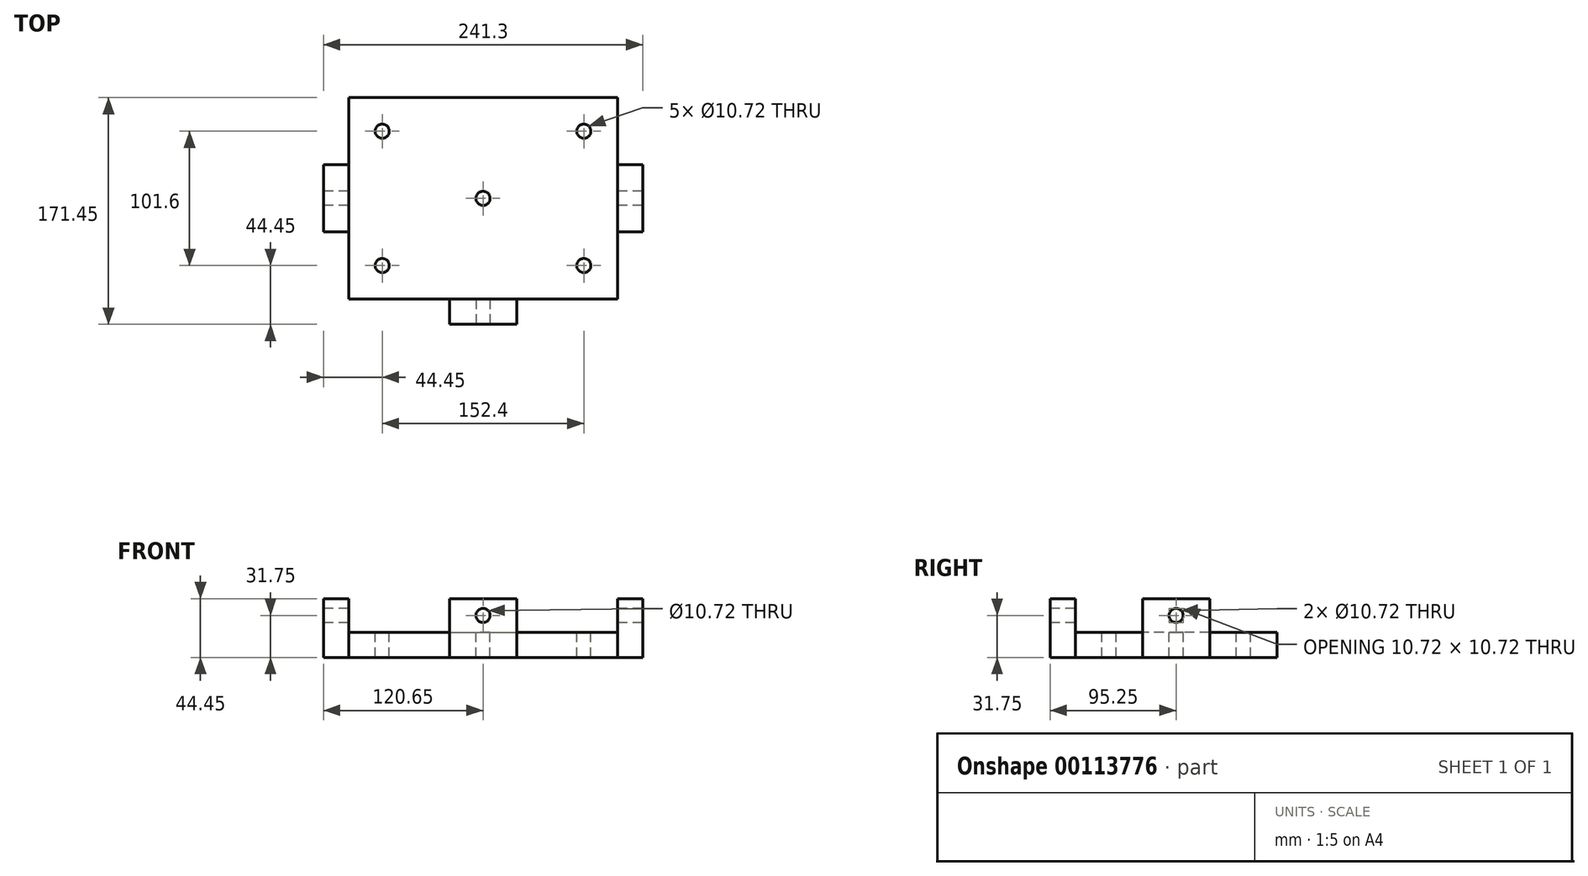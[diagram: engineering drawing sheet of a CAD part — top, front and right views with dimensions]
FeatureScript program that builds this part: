
annotation { "Feature Type Name" : "Feature", "Feature Type Description" : "" }
export const myFeature = defineFeature(function(context is Context, id is Id, definition is map)
    precondition{}
    {
        {
            var Q0;
            Q0=qCreatedBy(makeId("Top.planeOp"),FACE);
            var sketch = newSketch(context, id + "F0", { "sketchPlane" : qUnion([Q0])});
            skLineSegment(sketch, "E0.bottom", {"start": v(-101.6, 76.2) * mm, "end": v(101.6, 76.2) * mm});
            skLineSegment(sketch, "E0.top", {"start": v(-101.6, -76.2) * mm, "end": v(101.6, -76.2) * mm});
            skLineSegment(sketch, "E0.left", {"start": v(-101.6, 76.2) * mm, "end": v(-101.6, -76.2) * mm});
            skLineSegment(sketch, "E0.right", {"start": v(101.6, 76.2) * mm, "end": v(101.6, -76.2) * mm});
            skPoint(sketch, "E0.middle", {"position": v(0, 0) * mm});
            skLineSegment(sketch, "E1.bottom", {"start": v(-76.2, 50.8) * mm, "end": v(76.2, 50.8) * mm, "construction": true});
            skLineSegment(sketch, "E1.top", {"start": v(-76.2, -50.8) * mm, "end": v(76.2, -50.8) * mm, "construction": true});
            skLineSegment(sketch, "E1.left", {"start": v(-76.2, 50.8) * mm, "end": v(-76.2, -50.8) * mm, "construction": true});
            skLineSegment(sketch, "E1.right", {"start": v(76.2, 50.8) * mm, "end": v(76.2, -50.8) * mm, "construction": true});
            skSolve(sketch);
        }
        {
            var Q0;
            Q0=qSketchRegion(id+"F0",true);
            extrude(context, id + "F1", {"entities" : qUnion([Q0]), "depth" : 19.05 * mm});
        }
        {
            var Q0;
            Q0=makeQuery(id+"F1.opExtrude","CAP_FACE",FACE,{"disambiguationData":[OSD([sQuery(id+"F0.wireOp",EDGE,"E0.bottom"),sQuery(id+"F0.wireOp",EDGE,"E0.top"),sQuery(id+"F0.wireOp",EDGE,"E0.left"),sQuery(id+"F0.wireOp",EDGE,"E0.right")])],"isStart":false});
            var sketch = newSketch(context, id + "F2", { "sketchPlane" : qUnion([Q0])});
            skLineSegment(sketch, "E2.0", {"start": v(-76.2, 50.8) * mm, "end": v(76.2, 50.8) * mm, "construction": true});
            skLineSegment(sketch, "E3.0", {"start": v(-76.2, 50.8) * mm, "end": v(-76.2, -50.8) * mm, "construction": true});
            skLineSegment(sketch, "E4.0", {"start": v(-76.2, -50.8) * mm, "end": v(76.2, -50.8) * mm, "construction": true});
            skLineSegment(sketch, "E5.0", {"start": v(76.2, 50.8) * mm, "end": v(76.2, -50.8) * mm, "construction": true});
            skPoint(sketch, "E6", {"position": v(0, 0) * mm});
            skPoint(sketch, "E7", {"position": v(-76.2, 50.8) * mm});
            skPoint(sketch, "E8", {"position": v(76.2, 50.8) * mm});
            skPoint(sketch, "E9", {"position": v(76.2, -50.8) * mm});
            skPoint(sketch, "E10", {"position": v(-76.2, -50.8) * mm});
            skSolve(sketch);
        }
        {
            var Q0;
            Q0=sQuery(id+"F2.wireOp",VERTEX,"E7");
            var Q1;
            Q1=sQuery(id+"F2.wireOp",VERTEX,"E8");
            var Q2;
            Q2=sQuery(id+"F2.wireOp",VERTEX,"E6");
            var Q3;
            Q3=sQuery(id+"F2.wireOp",VERTEX,"E10");
            var Q4;
            Q4=sQuery(id+"F2.wireOp",VERTEX,"E9");
            var Q5;
            Q5=makeQuery(id+"F1.opExtrude","SWEPT_BODY",BODY,{"disambiguationData":[OSD([sQuery(id+"F0.wireOp",EDGE,"E0.bottom"),sQuery(id+"F0.wireOp",EDGE,"E0.top"),sQuery(id+"F0.wireOp",EDGE,"E0.left"),sQuery(id+"F0.wireOp",EDGE,"E0.right")])]});
            hole(context, id + "F3", {"style" : HoleStyle.SIMPLE, "endStyle" : HoleEndStyle.THROUGH, "standardTappedOrClearance" : lookupTablePath({ "standard" : "ANSI", "engagement" : "75%", "pitch" : "13 tpi", "size" : "1/2", "type" : "Tapped" }), "standardBlindInLast" : lookupTablePath({ "standard" : "ANSI", "engagement" : "75%", "pitch" : "13 tpi", "size" : "1/2", "type" : "Tapped" }), "holeDiameter" : 10.72 * mm, "locations" : qUnion([Q0, Q1, Q2, Q3, Q4]), "scope" : qUnion([Q5]), "isTappedThrough" : true, "majorDiameter" : 12.7 * mm, "showTappedDepth" : true});
        }
        {
            var Q0;
            Q0=makeQuery(id+"F0.imprint","IMPRINT",FACE,{"disambiguationData":[TD([[makeQuery(id+"F0.imprint","IMPRINT",EDGE,{"derivedFrom":sQuery(id+"F0.wireOp",EDGE,"E0.bottom")}),-1.0]])]});
            var sketch = newSketch(context, id + "F4", { "sketchPlane" : qUnion([Q0])});
            skLineSegment(sketch, "E11", {"start": v(-141.75, 0) * mm, "end": v(128.24, 0) * mm, "construction": true});
            skLineSegment(sketch, "E12", {"start": v(0, -93.67) * mm, "end": v(0, 85.34) * mm, "construction": true});
            skLineSegment(sketch, "E13.0", {"start": v(-141.75, -25.4) * mm, "end": v(128.24, -25.4) * mm, "construction": true});
            skLineSegment(sketch, "E14.0", {"start": v(-25.4, -93.67) * mm, "end": v(-25.4, 85.34) * mm, "construction": true});
            skLineSegment(sketch, "E15.0", {"start": v(-101.6, 76.2) * mm, "end": v(-101.6, -76.2) * mm, "construction": true});
            skLineSegment(sketch, "E16.0", {"start": v(-101.6, -76.2) * mm, "end": v(101.6, -76.2) * mm, "construction": true});
            skLineSegment(sketch, "E17.bottom", {"start": v(-101.6, -25.4) * mm, "end": v(-120.65, -25.4) * mm});
            skLineSegment(sketch, "E17.top", {"start": v(-101.6, 25.4) * mm, "end": v(-120.65, 25.4) * mm});
            skLineSegment(sketch, "E17.left", {"start": v(-101.6, -25.4) * mm, "end": v(-101.6, 25.4) * mm});
            skLineSegment(sketch, "E17.right", {"start": v(-120.65, -25.4) * mm, "end": v(-120.65, 25.4) * mm});
            skLineSegment(sketch, "E18.bottom", {"start": v(-25.4, -76.2) * mm, "end": v(25.4, -76.2) * mm});
            skLineSegment(sketch, "E18.top", {"start": v(-25.4, -95.25) * mm, "end": v(25.4, -95.25) * mm});
            skLineSegment(sketch, "E18.left", {"start": v(-25.4, -76.2) * mm, "end": v(-25.4, -95.25) * mm});
            skLineSegment(sketch, "E18.right", {"start": v(25.4, -76.2) * mm, "end": v(25.4, -95.25) * mm});
            skLineSegment(sketch, "E19.MirrorCS", {"start": v(101.6, -25.4) * mm, "end": v(120.65, -25.4) * mm});
            skLineSegment(sketch, "E20.MirrorCS", {"start": v(101.6, 25.4) * mm, "end": v(120.65, 25.4) * mm});
            skLineSegment(sketch, "E21.MirrorCS", {"start": v(120.65, -25.4) * mm, "end": v(120.65, 25.4) * mm});
            skLineSegment(sketch, "E22.MirrorCS", {"start": v(101.6, -25.4) * mm, "end": v(101.6, 25.4) * mm});
            skSolve(sketch);
        }
        {
            var Q0;
            Q0=qSketchRegion(id+"F4",true);
            extrude(context, id + "F5", {"entities" : qUnion([Q0]), "operationType" : NewBodyOperationType.ADD, "depth" : 44.45 * mm});
        }
        {
            var Q0;
            Q0=makeQuery(id+"F5.opExtrude","SWEPT_FACE",FACE,{"disambiguationData":[OSD([sQuery(id+"F4.wireOp",EDGE,"E18.top")])]});
            var sketch = newSketch(context, id + "F6", { "sketchPlane" : qUnion([Q0])});
            skLineSegment(sketch, "E23.0", {"start": v(-25.4, 0) * mm, "end": v(25.4, 0) * mm, "construction": true});
            skLineSegment(sketch, "E24.0", {"start": v(-25.4, 31.75) * mm, "end": v(25.4, 31.75) * mm, "construction": true});
            skPoint(sketch, "E25", {"position": v(0, 31.75) * mm});
            skSolve(sketch);
        }
        {
            var Q0;
            Q0=sQuery(id+"F6.wireOp",VERTEX,"E25");
            var Q1;
            Q1=makeQuery(id+"F1.opExtrude","SWEPT_BODY",BODY,{"disambiguationData":[OSD([sQuery(id+"F0.wireOp",EDGE,"E0.bottom"),sQuery(id+"F0.wireOp",EDGE,"E0.top"),sQuery(id+"F0.wireOp",EDGE,"E0.left"),sQuery(id+"F0.wireOp",EDGE,"E0.right")])]});
            hole(context, id + "F7", {"style" : HoleStyle.SIMPLE, "endStyle" : HoleEndStyle.THROUGH, "standardTappedOrClearance" : lookupTablePath({ "standard" : "ANSI", "engagement" : "75%", "pitch" : "13 tpi", "size" : "1/2", "type" : "Tapped" }), "standardBlindInLast" : lookupTablePath({ "standard" : "ANSI", "engagement" : "75%", "pitch" : "13 tpi", "size" : "1/2", "type" : "Tapped" }), "holeDiameter" : 10.72 * mm, "locations" : qUnion([Q0]), "scope" : qUnion([Q1]), "isTappedThrough" : true, "majorDiameter" : 12.7 * mm, "showTappedDepth" : true});
        }
        {
            var Q0;
            Q0=makeQuery(id+"F5.opExtrude","SWEPT_FACE",FACE,{"disambiguationData":[OSD([sQuery(id+"F4.wireOp",EDGE,"E17.right")])]});
            var sketch = newSketch(context, id + "F8", { "sketchPlane" : qUnion([Q0])});
            skLineSegment(sketch, "E26.0", {"start": v(25.4, 0) * mm, "end": v(-25.4, 0) * mm, "construction": true});
            skLineSegment(sketch, "E27.0", {"start": v(25.4, 31.75) * mm, "end": v(-25.4, 31.75) * mm, "construction": true});
            skPoint(sketch, "E28", {"position": v(0, 31.75) * mm});
            skSolve(sketch);
        }
        {
            var Q0;
            Q0=sQuery(id+"F8.wireOp",VERTEX,"E28");
            var Q1;
            Q1=makeQuery(id+"F1.opExtrude","SWEPT_BODY",BODY,{"disambiguationData":[OSD([sQuery(id+"F0.wireOp",EDGE,"E0.bottom"),sQuery(id+"F0.wireOp",EDGE,"E0.top"),sQuery(id+"F0.wireOp",EDGE,"E0.left"),sQuery(id+"F0.wireOp",EDGE,"E0.right")])]});
            hole(context, id + "F9", {"style" : HoleStyle.SIMPLE, "endStyle" : HoleEndStyle.THROUGH, "standardTappedOrClearance" : lookupTablePath({ "standard" : "ANSI", "engagement" : "75%", "pitch" : "13 tpi", "size" : "1/2", "type" : "Tapped" }), "standardBlindInLast" : lookupTablePath({ "standard" : "ANSI", "engagement" : "75%", "pitch" : "13 tpi", "size" : "1/2", "type" : "Tapped" }), "holeDiameter" : 10.72 * mm, "locations" : qUnion([Q0]), "scope" : qUnion([Q1]), "isTappedThrough" : true, "majorDiameter" : 12.7 * mm, "showTappedDepth" : true});
        }
    });
